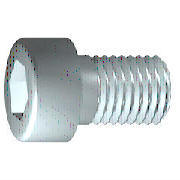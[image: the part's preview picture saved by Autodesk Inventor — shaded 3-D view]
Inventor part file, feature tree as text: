
AUTODESK INVENTOR PART (.ipt)
format: ipt  version: 2021 (Build 250183000, 183)  size: 199,680 bytes
history: native  units: mm (DEFAULTED — no unit token found)
features: other x3, fillet x2, extrude x1, chamfer x1, plane x1
ambient origin geometry x7: Origin, YZ Plane, XY Plane, X Axis, Y Axis, Z Axis, Center Point
bodies: Solid1 (feature_tree)
feature tree (8):
  other  "Corpo"
  extrude  "Fenda"  Depth=3.75mm
  fillet  "Raio de arredondamento1"  Radius=0.306825mm
  chamfer  "Chanfrar1"  Distance=3.0mm
  plane  "Work Plane1"
  fillet  "Fillet2"  Radius=1.3mm
  other  "Rascunho1"
  other  "Rascunho2"
